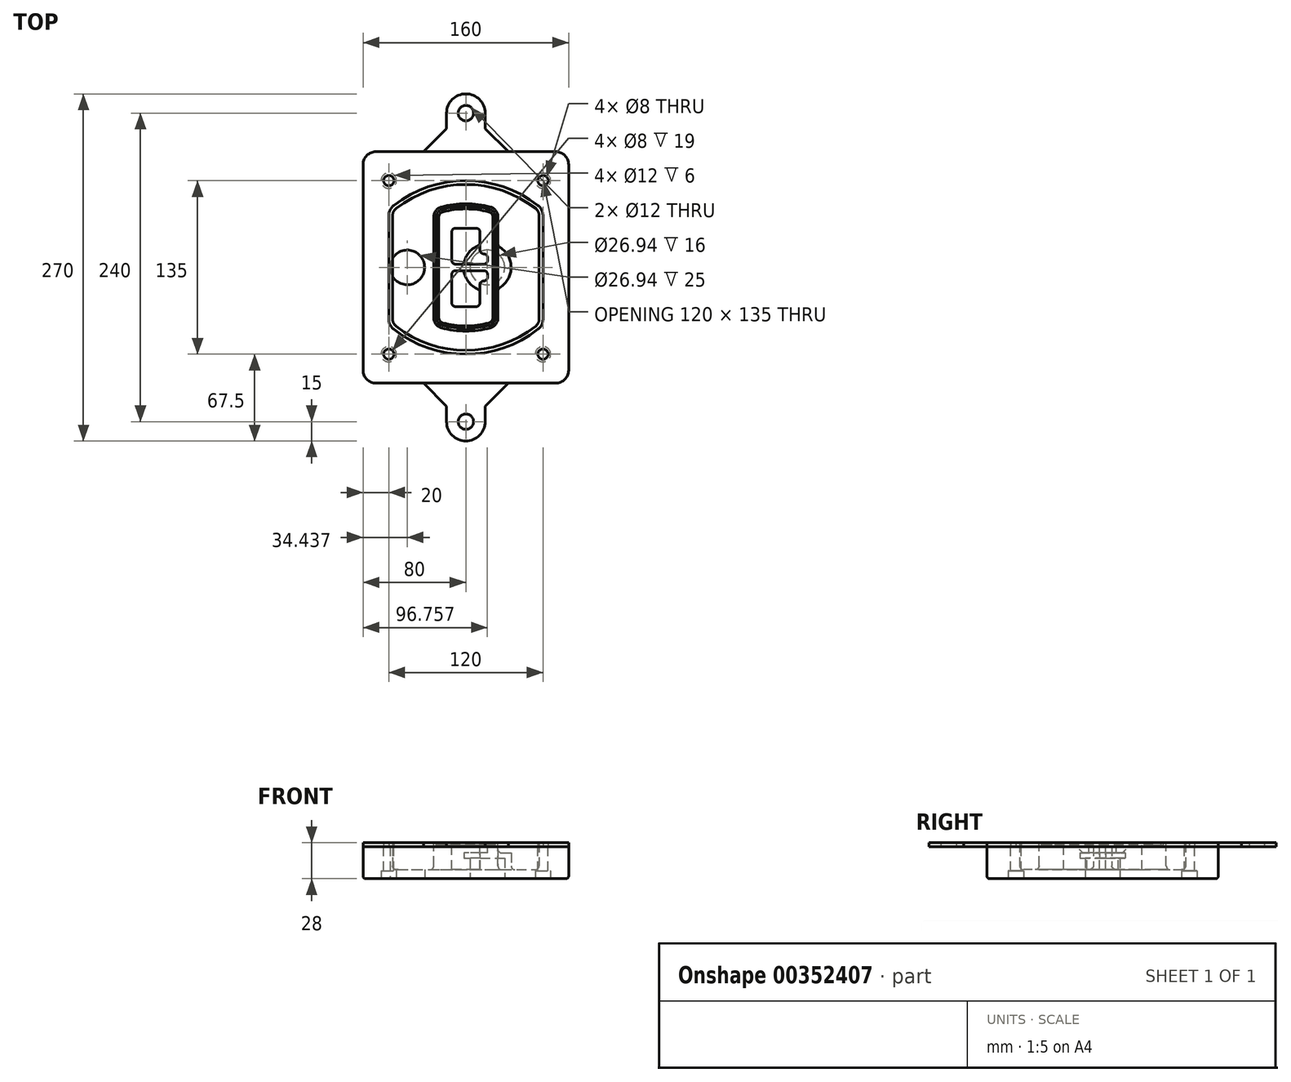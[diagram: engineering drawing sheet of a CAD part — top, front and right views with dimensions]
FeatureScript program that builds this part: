
annotation { "Feature Type Name" : "Feature", "Feature Type Description" : "" }
export const myFeature = defineFeature(function(context is Context, id is Id, definition is map)
    precondition{}
    {
        {
            var Q0;
            Q0=qCreatedBy(makeId("Top.planeOp"),FACE);
            var sketch = newSketch(context, id + "F0", { "sketchPlane" : qUnion([Q0])});
            skPoint(sketch, "E0.rect.middle", {"position": v(0, 0) * mm});
            skLineSegment(sketch, "E1.bottom", {"start": v(-70, -90) * mm, "end": v(70, -90) * mm});
            skLineSegment(sketch, "E1.top", {"start": v(-70, 90) * mm, "end": v(70, 90) * mm});
            skLineSegment(sketch, "E1.left", {"start": v(-80, -80) * mm, "end": v(-80, 80) * mm});
            skLineSegment(sketch, "E1.right", {"start": v(80, -80) * mm, "end": v(80, 80) * mm});
            skLineSegment(sketch, "E2", {"start": v(-80, 90) * mm, "end": v(80, -90) * mm, "construction": true});
            skLineSegment(sketch, "E3", {"start": v(80, 90) * mm, "end": v(-80, -90) * mm, "construction": true});
            skCircle(sketch, "E4", {"center": v(-60, 67.5) * mm, "radius": 4 * mm});
            skCircle(sketch, "E5", {"center": v(60, 67.5) * mm, "radius": 4 * mm});
            skCircle(sketch, "E6", {"center": v(60, -67.5) * mm, "radius": 4 * mm});
            skCircle(sketch, "E7", {"center": v(-60, -67.5) * mm, "radius": 4 * mm});
            skLineSegment(sketch, "E8", {"start": v(-60, 67.5) * mm, "end": v(60, 67.5) * mm, "construction": true});
            skLineSegment(sketch, "E9", {"start": v(60, 67.5) * mm, "end": v(60, -67.5) * mm, "construction": true});
            skLineSegment(sketch, "E10", {"start": v(60, -67.5) * mm, "end": v(-60, -67.5) * mm, "construction": true});
            skLineSegment(sketch, "E11", {"start": v(-60, -67.5) * mm, "end": v(-60, 67.5) * mm, "construction": true});
            skLineSegment(sketch, "E12", {"start": v(-60, 40.3) * mm, "end": v(-60, -40.3) * mm});
            skLineSegment(sketch, "E13", {"start": v(60, 40.3) * mm, "end": v(60, -40.3) * mm});
            skArc(sketch, "E14", {"start": v(56.15, 48.18) * mm, "mid": v(0, 67.5) * mm, "end": v(-56.15, 48.18) * mm});
            skArc(sketch, "E15", {"start": v(-56.15, -48.18) * mm, "mid": v(0, -67.5) * mm, "end": v(56.15, -48.18) * mm});
            skLineSegment(sketch, "E16", {"start": v(-60, 0) * mm, "end": v(60, 0) * mm, "construction": true});
            skPoint(sketch, "E17.visualSharp", {"position": v(-60, -45) * mm});
            skArc(sketch, "E17.filletArc", {"start": v(-60, -40.3) * mm, "mid": v(-58.99, -44.68) * mm, "end": v(-56.15, -48.18) * mm});
            skPoint(sketch, "E18.visualSharp", {"position": v(-60, 45) * mm});
            skArc(sketch, "E18.filletArc", {"start": v(-56.15, 48.18) * mm, "mid": v(-58.99, 44.68) * mm, "end": v(-60, 40.3) * mm});
            skPoint(sketch, "E19.visualSharp", {"position": v(60, 45) * mm});
            skArc(sketch, "E19.filletArc", {"start": v(60, 40.3) * mm, "mid": v(58.99, 44.68) * mm, "end": v(56.15, 48.18) * mm});
            skPoint(sketch, "E20.visualSharp", {"position": v(60, -45) * mm});
            skArc(sketch, "E20.filletArc", {"start": v(56.15, -48.18) * mm, "mid": v(58.99, -44.68) * mm, "end": v(60, -40.3) * mm});
            skPoint(sketch, "E21.visualSharp", {"position": v(-80, 90) * mm});
            skArc(sketch, "E21.filletArc", {"start": v(-70, 90) * mm, "mid": v(-77.07, 87.07) * mm, "end": v(-80, 80) * mm});
            skPoint(sketch, "E22.visualSharp", {"position": v(80, 90) * mm});
            skArc(sketch, "E22.filletArc", {"start": v(80, 80) * mm, "mid": v(77.07, 87.07) * mm, "end": v(70, 90) * mm});
            skPoint(sketch, "E23.visualSharp", {"position": v(80, -90) * mm});
            skArc(sketch, "E23.filletArc", {"start": v(70, -90) * mm, "mid": v(77.07, -87.07) * mm, "end": v(80, -80) * mm});
            skPoint(sketch, "E24.visualSharp", {"position": v(-80, -90) * mm});
            skArc(sketch, "E24.filletArc", {"start": v(-80, -80) * mm, "mid": v(-77.07, -87.07) * mm, "end": v(-70, -90) * mm});
            skArc(sketch, "E25.0", {"start": v(57, 40.3) * mm, "mid": v(56.3, 43.36) * mm, "end": v(54.3, 45.81) * mm});
            skLineSegment(sketch, "E25.1", {"start": v(57, 40.3) * mm, "end": v(57, -40.3) * mm});
            skArc(sketch, "E25.2", {"start": v(54.3, -45.81) * mm, "mid": v(56.3, -43.36) * mm, "end": v(57, -40.3) * mm});
            skArc(sketch, "E25.3", {"start": v(-54.3, -45.81) * mm, "mid": v(0, -64.5) * mm, "end": v(54.3, -45.81) * mm});
            skArc(sketch, "E25.4", {"start": v(-57, -40.3) * mm, "mid": v(-56.3, -43.36) * mm, "end": v(-54.3, -45.81) * mm});
            skArc(sketch, "E25.5", {"start": v(54.3, 45.81) * mm, "mid": v(0, 64.5) * mm, "end": v(-54.3, 45.81) * mm});
            skLineSegment(sketch, "E25.6", {"start": v(-57, 40.3) * mm, "end": v(-57, -40.3) * mm});
            skArc(sketch, "E25.7", {"start": v(-54.3, 45.81) * mm, "mid": v(-56.3, 43.36) * mm, "end": v(-57, 40.3) * mm});
            skArc(sketch, "E26.0", {"start": v(-58.62, 51.33) * mm, "mid": v(-62.58, 46.43) * mm, "end": v(-64, 40.3) * mm});
            skArc(sketch, "E26.1", {"start": v(58.62, 51.33) * mm, "mid": v(0, 71.5) * mm, "end": v(-58.62, 51.33) * mm});
            skArc(sketch, "E26.2", {"start": v(64, 40.3) * mm, "mid": v(62.58, 46.43) * mm, "end": v(58.62, 51.33) * mm});
            skLineSegment(sketch, "E26.3", {"start": v(64, 40.3) * mm, "end": v(64, -40.3) * mm});
            skArc(sketch, "E26.4", {"start": v(58.62, -51.33) * mm, "mid": v(62.58, -46.43) * mm, "end": v(64, -40.3) * mm});
            skLineSegment(sketch, "E26.5", {"start": v(-64, 40.3) * mm, "end": v(-64, -40.3) * mm});
            skArc(sketch, "E26.6", {"start": v(-58.62, -51.33) * mm, "mid": v(0, -71.5) * mm, "end": v(58.62, -51.33) * mm});
            skArc(sketch, "E26.7", {"start": v(-64, -40.3) * mm, "mid": v(-62.58, -46.43) * mm, "end": v(-58.62, -51.33) * mm});
            skSolve(sketch);
        }
        {
            var Q0;
            Q0=makeQuery(id+"F0.imprint","IMPRINT",FACE,{"disambiguationData":[TD([[makeQuery(id+"F0.imprint","IMPRINT",EDGE,{"derivedFrom":sQuery(id+"F0.wireOp",EDGE,"E1.bottom")}),1.0]])]});
            var Q1;
            Q1=makeQuery(id+"F0.imprint","IMPRINT",FACE,{"disambiguationData":[TD([[makeQuery(id+"F0.imprint","IMPRINT",EDGE,{"derivedFrom":sQuery(id+"F0.wireOp",EDGE,"E12")}),1.0]])]});
            var Q2;
            Q2=makeQuery(id+"F0.imprint","IMPRINT",FACE,{"disambiguationData":[TD([[makeQuery(id+"F0.imprint","IMPRINT",EDGE,{"derivedFrom":sQuery(id+"F0.wireOp",EDGE,"E25.0")}),1.0]])]});
            var Q3;
            Q3=makeQuery(id+"F0.imprint","IMPRINT",FACE,{"disambiguationData":[TD([[makeQuery(id+"F0.imprint","IMPRINT",EDGE,{"derivedFrom":sQuery(id+"F0.wireOp",EDGE,"E12")}),-1.0]])]});
            extrude(context, id + "F1", {"entities" : qUnion([Q0, Q1, Q2, Q3]), "oppositeDirection" : true, "depth" : 25 * mm});
        }
        {
            var Q0;
            Q0=makeQuery(id+"F0.imprint","IMPRINT",FACE,{"disambiguationData":[TD([[makeQuery(id+"F0.imprint","IMPRINT",EDGE,{"derivedFrom":sQuery(id+"F0.wireOp",EDGE,"E12")}),1.0]])]});
            extrude(context, id + "F2", {"entities" : qUnion([Q0]), "operationType" : NewBodyOperationType.ADD, "depth" : 3 * mm});
        }
        {
            var Q0;
            Q0=makeQuery(id+"F0.imprint","IMPRINT",FACE,{"disambiguationData":[TD([[makeQuery(id+"F0.imprint","IMPRINT",EDGE,{"derivedFrom":sQuery(id+"F0.wireOp",EDGE,"E25.0")}),1.0]])]});
            extrude(context, id + "F3", {"entities" : qUnion([Q0]), "operationType" : NewBodyOperationType.REMOVE, "oppositeDirection" : true, "depth" : 18 * mm});
        }
        {
            var Q0;
            Q0=makeQuery(id+"F2.opExtrude","CAP_FACE",FACE,{"disambiguationData":[OSD([sQuery(id+"F0.wireOp",EDGE,"E12"),sQuery(id+"F0.wireOp",EDGE,"E13"),sQuery(id+"F0.wireOp",EDGE,"E14"),sQuery(id+"F0.wireOp",EDGE,"E15"),sQuery(id+"F0.wireOp",EDGE,"E17.filletArc"),sQuery(id+"F0.wireOp",EDGE,"E18.filletArc"),sQuery(id+"F0.wireOp",EDGE,"E19.filletArc"),sQuery(id+"F0.wireOp",EDGE,"E20.filletArc"),sQuery(id+"F0.wireOp",EDGE,"E25.0"),sQuery(id+"F0.wireOp",EDGE,"E25.1"),sQuery(id+"F0.wireOp",EDGE,"E25.2"),sQuery(id+"F0.wireOp",EDGE,"E25.3"),sQuery(id+"F0.wireOp",EDGE,"E25.4"),sQuery(id+"F0.wireOp",EDGE,"E25.5"),sQuery(id+"F0.wireOp",EDGE,"E25.6"),sQuery(id+"F0.wireOp",EDGE,"E25.7")])],"isStart":false});
            var sketch = newSketch(context, id + "F4", { "sketchPlane" : qUnion([Q0])});
            skArc(sketch, "E27.0", {"start": v(-19.08, -46.97) * mm, "mid": v(0, -49.5) * mm, "end": v(19.08, -46.97) * mm});
            skArc(sketch, "E28.0", {"start": v(19.08, 46.97) * mm, "mid": v(0, 49.5) * mm, "end": v(-19.08, 46.97) * mm});
            skLineSegment(sketch, "E29", {"start": v(-25, 39.25) * mm, "end": v(-25, -39.25) * mm});
            skLineSegment(sketch, "E30", {"start": v(25, 39.25) * mm, "end": v(25, -39.25) * mm});
            skLineSegment(sketch, "E31", {"start": v(-25, 45.1) * mm, "end": v(25, 45.1) * mm, "construction": true});
            skLineSegment(sketch, "E32", {"start": v(-25, -45.1) * mm, "end": v(25, -45.1) * mm, "construction": true});
            skPoint(sketch, "E33.visualSharp", {"position": v(-25, 45.1) * mm});
            skArc(sketch, "E33.filletArc", {"start": v(-19.08, 46.97) * mm, "mid": v(-23.35, 44.11) * mm, "end": v(-25, 39.25) * mm});
            skPoint(sketch, "E34.visualSharp", {"position": v(25, 45.1) * mm});
            skArc(sketch, "E34.filletArc", {"start": v(25, 39.25) * mm, "mid": v(23.35, 44.11) * mm, "end": v(19.08, 46.97) * mm});
            skPoint(sketch, "E35.visualSharp", {"position": v(25, -45.1) * mm});
            skArc(sketch, "E35.filletArc", {"start": v(19.08, -46.97) * mm, "mid": v(23.35, -44.11) * mm, "end": v(25, -39.25) * mm});
            skPoint(sketch, "E36.visualSharp", {"position": v(-25, -45.1) * mm});
            skArc(sketch, "E36.filletArc", {"start": v(-25, -39.25) * mm, "mid": v(-23.35, -44.11) * mm, "end": v(-19.08, -46.97) * mm});
            skArc(sketch, "E37.0", {"start": v(54.3, 45.81) * mm, "mid": v(0, 64.5) * mm, "end": v(-54.3, 45.81) * mm});
            skArc(sketch, "E37.1", {"start": v(-54.3, 45.81) * mm, "mid": v(-56.3, 43.36) * mm, "end": v(-57, 40.3) * mm});
            skLineSegment(sketch, "E37.2", {"start": v(-57, 40.3) * mm, "end": v(-57, -40.3) * mm});
            skArc(sketch, "E37.3", {"start": v(-57, -40.3) * mm, "mid": v(-56.3, -43.36) * mm, "end": v(-54.3, -45.81) * mm});
            skArc(sketch, "E37.4", {"start": v(-54.3, -45.81) * mm, "mid": v(0, -64.5) * mm, "end": v(54.3, -45.81) * mm});
            skArc(sketch, "E37.5", {"start": v(54.3, -45.81) * mm, "mid": v(56.3, -43.36) * mm, "end": v(57, -40.3) * mm});
            skLineSegment(sketch, "E37.6", {"start": v(57, 40.3) * mm, "end": v(57, -40.3) * mm});
            skArc(sketch, "E37.7", {"start": v(57, 40.3) * mm, "mid": v(56.3, 43.36) * mm, "end": v(54.3, 45.81) * mm});
            skLineSegment(sketch, "E38.0", {"start": v(23, 39.25) * mm, "end": v(23, -39.25) * mm});
            skArc(sketch, "E38.1", {"start": v(18.56, -45.04) * mm, "mid": v(21.76, -42.9) * mm, "end": v(23, -39.25) * mm});
            skArc(sketch, "E38.2", {"start": v(-18.56, -45.04) * mm, "mid": v(0, -47.5) * mm, "end": v(18.56, -45.04) * mm});
            skArc(sketch, "E38.3", {"start": v(-23, -39.25) * mm, "mid": v(-21.76, -42.9) * mm, "end": v(-18.56, -45.04) * mm});
            skLineSegment(sketch, "E38.4", {"start": v(-23, 39.25) * mm, "end": v(-23, -39.25) * mm});
            skArc(sketch, "E38.5", {"start": v(23, 39.25) * mm, "mid": v(21.76, 42.9) * mm, "end": v(18.56, 45.04) * mm});
            skArc(sketch, "E38.6", {"start": v(-18.56, 45.04) * mm, "mid": v(-21.76, 42.9) * mm, "end": v(-23, 39.25) * mm});
            skArc(sketch, "E38.7", {"start": v(18.56, 45.04) * mm, "mid": v(0, 47.5) * mm, "end": v(-18.56, 45.04) * mm});
            skArc(sketch, "E39.0", {"start": v(21, 39.25) * mm, "mid": v(20.18, 41.68) * mm, "end": v(18.04, 43.1) * mm});
            skLineSegment(sketch, "E39.1", {"start": v(21, 39.25) * mm, "end": v(21, -39.25) * mm});
            skArc(sketch, "E39.2", {"start": v(18.04, -43.1) * mm, "mid": v(20.18, -41.68) * mm, "end": v(21, -39.25) * mm});
            skArc(sketch, "E39.3", {"start": v(-18.04, -43.1) * mm, "mid": v(0, -45.5) * mm, "end": v(18.04, -43.1) * mm});
            skArc(sketch, "E39.4", {"start": v(-21, -39.25) * mm, "mid": v(-20.18, -41.68) * mm, "end": v(-18.04, -43.1) * mm});
            skArc(sketch, "E39.5", {"start": v(18.04, 43.1) * mm, "mid": v(0, 45.5) * mm, "end": v(-18.04, 43.1) * mm});
            skLineSegment(sketch, "E39.6", {"start": v(-21, 39.25) * mm, "end": v(-21, -39.25) * mm});
            skArc(sketch, "E39.7", {"start": v(-18.04, 43.1) * mm, "mid": v(-20.18, 41.68) * mm, "end": v(-21, 39.25) * mm});
            skLineSegment(sketch, "E40", {"start": v(-25, 0) * mm, "end": v(25, 0) * mm, "construction": true});
            skLineSegment(sketch, "E41", {"start": v(-11, 5.5) * mm, "end": v(-11, 27.5) * mm});
            skLineSegment(sketch, "E42", {"start": v(-8, 30.5) * mm, "end": v(8, 30.5) * mm});
            skLineSegment(sketch, "E43", {"start": v(11, 27.5) * mm, "end": v(11, 13.5) * mm});
            skLineSegment(sketch, "E44", {"start": v(14, 10.5) * mm, "end": v(14, 10.5) * mm});
            skLineSegment(sketch, "E45", {"start": v(17, 7.5) * mm, "end": v(17, 5.5) * mm});
            skLineSegment(sketch, "E46", {"start": v(14, 2.5) * mm, "end": v(-8, 2.5) * mm});
            skPoint(sketch, "E47.visualSharp", {"position": v(-11, 30.5) * mm});
            skArc(sketch, "E47.filletArc", {"start": v(-8, 30.5) * mm, "mid": v(-10.12, 29.62) * mm, "end": v(-11, 27.5) * mm});
            skPoint(sketch, "E48.visualSharp", {"position": v(11, 30.5) * mm});
            skArc(sketch, "E48.filletArc", {"start": v(11, 27.5) * mm, "mid": v(10.12, 29.62) * mm, "end": v(8, 30.5) * mm});
            skPoint(sketch, "E49.visualSharp", {"position": v(11, 10.5) * mm});
            skArc(sketch, "E49.filletArc", {"start": v(11, 13.5) * mm, "mid": v(11.88, 11.38) * mm, "end": v(14, 10.5) * mm});
            skPoint(sketch, "E50.visualSharp", {"position": v(17, 10.5) * mm});
            skArc(sketch, "E50.filletArc", {"start": v(17, 7.5) * mm, "mid": v(16.12, 9.62) * mm, "end": v(14, 10.5) * mm});
            skPoint(sketch, "E51.visualSharp", {"position": v(17, 2.5) * mm});
            skArc(sketch, "E51.filletArc", {"start": v(14, 2.5) * mm, "mid": v(16.12, 3.38) * mm, "end": v(17, 5.5) * mm});
            skPoint(sketch, "E52.visualSharp", {"position": v(-11, 2.5) * mm});
            skArc(sketch, "E52.filletArc", {"start": v(-11, 5.5) * mm, "mid": v(-10.12, 3.38) * mm, "end": v(-8, 2.5) * mm});
            skLineSegment(sketch, "E53.0.MirrorCS", {"start": v(14, -2.5) * mm, "end": v(-8, -2.5) * mm});
            skArc(sketch, "E54.0.MirrorCS", {"start": v(-11, -5.5) * mm, "mid": v(-10.12, -3.38) * mm, "end": v(-8, -2.5) * mm});
            skLineSegment(sketch, "E55.0.MirrorCS", {"start": v(-11, -5.5) * mm, "end": v(-11, -27.5) * mm});
            skArc(sketch, "E56.0.MirrorCS", {"start": v(-8, -30.5) * mm, "mid": v(-10.12, -29.62) * mm, "end": v(-11, -27.5) * mm});
            skLineSegment(sketch, "E57.0.MirrorCS", {"start": v(-8, -30.5) * mm, "end": v(8, -30.5) * mm});
            skArc(sketch, "E58.0.MirrorCS", {"start": v(11, -27.5) * mm, "mid": v(10.12, -29.62) * mm, "end": v(8, -30.5) * mm});
            skLineSegment(sketch, "E59.0.MirrorCS", {"start": v(11, -27.5) * mm, "end": v(11, -13.5) * mm});
            skArc(sketch, "E60.0.MirrorCS", {"start": v(11, -13.5) * mm, "mid": v(11.88, -11.38) * mm, "end": v(14, -10.5) * mm});
            skArc(sketch, "E61.0.MirrorCS", {"start": v(17, -7.5) * mm, "mid": v(16.12, -9.62) * mm, "end": v(14, -10.5) * mm});
            skLineSegment(sketch, "E62.0.MirrorCS", {"start": v(17, -7.5) * mm, "end": v(17, -5.5) * mm});
            skArc(sketch, "E63.0.MirrorCS", {"start": v(14, -2.5) * mm, "mid": v(16.12, -3.38) * mm, "end": v(17, -5.5) * mm});
            skSolve(sketch);
        }
        {
            var Q0;
            Q0=makeQuery(id+"F4.imprint","IMPRINT",FACE,{"disambiguationData":[TD([[makeQuery(id+"F4.imprint","IMPRINT",EDGE,{"derivedFrom":sQuery(id+"F4.wireOp",EDGE,"E27.0")}),1.0]])]});
            var Q1;
            Q1=makeQuery(id+"F4.imprint","IMPRINT",FACE,{"disambiguationData":[TD([[makeQuery(id+"F4.imprint","IMPRINT",EDGE,{"derivedFrom":sQuery(id+"F4.wireOp",EDGE,"E38.0")}),-1.0]])]});
            var Q2;
            Q2=makeQuery(id+"F4.imprint","IMPRINT",FACE,{"disambiguationData":[TD([[makeQuery(id+"F4.imprint","IMPRINT",EDGE,{"derivedFrom":sQuery(id+"F4.wireOp",EDGE,"E39.0")}),1.0]])]});
            extrude(context, id + "F5", {"entities" : qUnion([Q0, Q1, Q2]), "operationType" : NewBodyOperationType.ADD, "endBound" : BoundingType.UP_TO_NEXT, "oppositeDirection" : true, "depth" : 25 * mm});
        }
        {
            var Q0;
            Q0=makeQuery(id+"F4.imprint","IMPRINT",FACE,{"disambiguationData":[TD([[makeQuery(id+"F4.imprint","IMPRINT",EDGE,{"derivedFrom":sQuery(id+"F4.wireOp",EDGE,"E38.0")}),-1.0]])]});
            extrude(context, id + "F6", {"entities" : qUnion([Q0]), "operationType" : NewBodyOperationType.REMOVE, "oppositeDirection" : true, "depth" : 2 * mm});
        }
        {
            var Q0;
            Q0=makeQuery(id+"F1.opExtrude","CAP_FACE",FACE,{"disambiguationData":[OSD([sQuery(id+"F0.wireOp",EDGE,"E1.bottom"),sQuery(id+"F0.wireOp",EDGE,"E1.top"),sQuery(id+"F0.wireOp",EDGE,"E1.left"),sQuery(id+"F0.wireOp",EDGE,"E1.right"),sQuery(id+"F0.wireOp",EDGE,"E4"),sQuery(id+"F0.wireOp",EDGE,"E5"),sQuery(id+"F0.wireOp",EDGE,"E6"),sQuery(id+"F0.wireOp",EDGE,"E7"),sQuery(id+"F0.wireOp",EDGE,"E21.filletArc"),sQuery(id+"F0.wireOp",EDGE,"E22.filletArc"),sQuery(id+"F0.wireOp",EDGE,"E23.filletArc"),sQuery(id+"F0.wireOp",EDGE,"E24.filletArc")])],"isStart":false});
            var sketch = newSketch(context, id + "F7", { "sketchPlane" : qUnion([Q0])});
            skCircle(sketch, "E64", {"center": v(16.76, 0) * mm, "radius": 13.47 * mm});
            skCircle(sketch, "E65", {"center": v(-45.56, 0) * mm, "radius": 13.47 * mm});
            skLineSegment(sketch, "E66", {"start": v(80, 0) * mm, "end": v(-80, 0) * mm});
            skCircle(sketch, "E67", {"center": v(16.76, 0) * mm, "radius": 18.47 * mm});
            skCircle(sketch, "E68", {"center": v(60, -67.5) * mm, "radius": 6 * mm});
            skCircle(sketch, "E69", {"center": v(-60, -67.5) * mm, "radius": 6 * mm});
            skCircle(sketch, "E70", {"center": v(-60, 67.5) * mm, "radius": 6 * mm});
            skCircle(sketch, "E71", {"center": v(60, 67.5) * mm, "radius": 6 * mm});
            skSolve(sketch);
        }
        {
            var Q0;
            {var subQ1=sQuery(id+"F7.wireOp",EDGE,"E66");var subQ4=sQuery(id+"F7.wireOp",EDGE,"E64");var subQ6=makeQuery(id+"F7.imprint","INTERSECT",VERTEX,{"disambiguationData":[OD(0.0)],"derivedFrom":[subQ4,subQ1]});Q0=makeQuery(id+"F7.imprint","IMPRINT",FACE,{"disambiguationData":[TD([[makeQuery(id+"F7.imprint","IMPRINT",EDGE,{"disambiguationData":[TD([[subQ6,-1.0]])],"derivedFrom":subQ4}),-1.0]])]});}
            var Q1;
            {var subQ0=sQuery(id+"F7.wireOp",EDGE,"E66");var subQ1=sQuery(id+"F7.wireOp",EDGE,"E64");var subQ3=makeQuery(id+"F7.imprint","INTERSECT",VERTEX,{"disambiguationData":[OD(0.0)],"derivedFrom":[subQ1,subQ0]});Q1=makeQuery(id+"F7.imprint","IMPRINT",FACE,{"disambiguationData":[TD([[makeQuery(id+"F7.imprint","IMPRINT",EDGE,{"disambiguationData":[TD([[subQ3,-1.0]])],"derivedFrom":subQ1}),1.0]])]});}
            var Q2;
            {var subQ0=sQuery(id+"F7.wireOp",EDGE,"E66");var subQ1=sQuery(id+"F7.wireOp",EDGE,"E64");var subQ3=makeQuery(id+"F7.imprint","INTERSECT",VERTEX,{"disambiguationData":[OD(0.0)],"derivedFrom":[subQ1,subQ0]});Q2=makeQuery(id+"F7.imprint","IMPRINT",FACE,{"disambiguationData":[TD([[makeQuery(id+"F7.imprint","IMPRINT",EDGE,{"disambiguationData":[TD([[subQ3,1.0]])],"derivedFrom":subQ1}),1.0]])]});}
            var Q3;
            {var subQ1=sQuery(id+"F7.wireOp",EDGE,"E66");var subQ4=sQuery(id+"F7.wireOp",EDGE,"E64");var subQ6=makeQuery(id+"F7.imprint","INTERSECT",VERTEX,{"disambiguationData":[OD(0.0)],"derivedFrom":[subQ4,subQ1]});Q3=makeQuery(id+"F7.imprint","IMPRINT",FACE,{"disambiguationData":[TD([[makeQuery(id+"F7.imprint","IMPRINT",EDGE,{"disambiguationData":[TD([[subQ6,1.0]])],"derivedFrom":subQ4}),-1.0]])]});}
            extrude(context, id + "F8", {"entities" : qUnion([Q0, Q1, Q2, Q3]), "operationType" : NewBodyOperationType.ADD, "oppositeDirection" : true, "depth" : 20 * mm});
        }
        {
            var Q0;
            {var subQ0=sQuery(id+"F7.wireOp",EDGE,"E66");var subQ1=sQuery(id+"F7.wireOp",EDGE,"E64");var subQ3=makeQuery(id+"F7.imprint","INTERSECT",VERTEX,{"disambiguationData":[OD(0.0)],"derivedFrom":[subQ1,subQ0]});Q0=makeQuery(id+"F7.imprint","IMPRINT",FACE,{"disambiguationData":[TD([[makeQuery(id+"F7.imprint","IMPRINT",EDGE,{"disambiguationData":[TD([[subQ3,-1.0]])],"derivedFrom":subQ1}),1.0]])]});}
            var Q1;
            {var subQ0=sQuery(id+"F7.wireOp",EDGE,"E66");var subQ1=sQuery(id+"F7.wireOp",EDGE,"E64");var subQ3=makeQuery(id+"F7.imprint","INTERSECT",VERTEX,{"disambiguationData":[OD(0.0)],"derivedFrom":[subQ1,subQ0]});Q1=makeQuery(id+"F7.imprint","IMPRINT",FACE,{"disambiguationData":[TD([[makeQuery(id+"F7.imprint","IMPRINT",EDGE,{"disambiguationData":[TD([[subQ3,1.0]])],"derivedFrom":subQ1}),1.0]])]});}
            extrude(context, id + "F9", {"entities" : qUnion([Q0, Q1]), "operationType" : NewBodyOperationType.REMOVE, "oppositeDirection" : true, "depth" : 16 * mm});
        }
        {
            var Q0;
            {var subQ0=sQuery(id+"F7.wireOp",EDGE,"E66");var subQ1=sQuery(id+"F7.wireOp",EDGE,"E65");var subQ3=makeQuery(id+"F7.imprint","INTERSECT",VERTEX,{"disambiguationData":[OD(0.0)],"derivedFrom":[subQ1,subQ0]});Q0=makeQuery(id+"F7.imprint","IMPRINT",FACE,{"disambiguationData":[TD([[makeQuery(id+"F7.imprint","IMPRINT",EDGE,{"disambiguationData":[TD([[subQ3,-1.0]])],"derivedFrom":subQ1}),1.0]])]});}
            var Q1;
            {var subQ0=sQuery(id+"F7.wireOp",EDGE,"E66");var subQ1=sQuery(id+"F7.wireOp",EDGE,"E65");var subQ3=makeQuery(id+"F7.imprint","INTERSECT",VERTEX,{"disambiguationData":[OD(0.0)],"derivedFrom":[subQ1,subQ0]});Q1=makeQuery(id+"F7.imprint","IMPRINT",FACE,{"disambiguationData":[TD([[makeQuery(id+"F7.imprint","IMPRINT",EDGE,{"disambiguationData":[TD([[subQ3,1.0]])],"derivedFrom":subQ1}),1.0]])]});}
            extrude(context, id + "F10", {"entities" : qUnion([Q0, Q1]), "operationType" : NewBodyOperationType.REMOVE, "oppositeDirection" : true, "depth" : 25 * mm});
        }
        {
            var Q0;
            Q0=makeQuery(id+"F7.imprint","IMPRINT",FACE,{"disambiguationData":[TD([[makeQuery(id+"F7.imprint","IMPRINT",EDGE,{"derivedFrom":sQuery(id+"F7.wireOp",EDGE,"E68")}),1.0]])]});
            var Q1;
            Q1=makeQuery(id+"F7.imprint","IMPRINT",FACE,{"disambiguationData":[TD([[makeQuery(id+"F7.imprint","IMPRINT",EDGE,{"derivedFrom":makeQuery(id+"F1.opExtrude","CAP_EDGE",EDGE,{"disambiguationData":[OSD([sQuery(id+"F0.wireOp",EDGE,"E5")])],"isStart":false})}),-1.0]])]});
            var Q2;
            Q2=makeQuery(id+"F7.imprint","IMPRINT",FACE,{"disambiguationData":[TD([[makeQuery(id+"F7.imprint","IMPRINT",EDGE,{"derivedFrom":sQuery(id+"F7.wireOp",EDGE,"E69")}),1.0]])]});
            var Q3;
            Q3=makeQuery(id+"F7.imprint","IMPRINT",FACE,{"disambiguationData":[TD([[makeQuery(id+"F7.imprint","IMPRINT",EDGE,{"derivedFrom":makeQuery(id+"F1.opExtrude","CAP_EDGE",EDGE,{"disambiguationData":[OSD([sQuery(id+"F0.wireOp",EDGE,"E4")])],"isStart":false})}),-1.0]])]});
            var Q4;
            Q4=makeQuery(id+"F7.imprint","IMPRINT",FACE,{"disambiguationData":[TD([[makeQuery(id+"F7.imprint","IMPRINT",EDGE,{"derivedFrom":sQuery(id+"F7.wireOp",EDGE,"E70")}),1.0]])]});
            var Q5;
            Q5=makeQuery(id+"F7.imprint","IMPRINT",FACE,{"disambiguationData":[TD([[makeQuery(id+"F7.imprint","IMPRINT",EDGE,{"derivedFrom":makeQuery(id+"F1.opExtrude","CAP_EDGE",EDGE,{"disambiguationData":[OSD([sQuery(id+"F0.wireOp",EDGE,"E7")])],"isStart":false})}),-1.0]])]});
            var Q6;
            Q6=makeQuery(id+"F7.imprint","IMPRINT",FACE,{"disambiguationData":[TD([[makeQuery(id+"F7.imprint","IMPRINT",EDGE,{"derivedFrom":sQuery(id+"F7.wireOp",EDGE,"E71")}),1.0]])]});
            var Q7;
            Q7=makeQuery(id+"F7.imprint","IMPRINT",FACE,{"disambiguationData":[TD([[makeQuery(id+"F7.imprint","IMPRINT",EDGE,{"derivedFrom":makeQuery(id+"F1.opExtrude","CAP_EDGE",EDGE,{"disambiguationData":[OSD([sQuery(id+"F0.wireOp",EDGE,"E6")])],"isStart":false})}),-1.0]])]});
            extrude(context, id + "F11", {"entities" : qUnion([Q0, Q1, Q2, Q3, Q4, Q5, Q6, Q7]), "operationType" : NewBodyOperationType.REMOVE, "oppositeDirection" : true, "depth" : 6 * mm});
        }
        {
            var Q0;
            Q0=makeQuery(id+"F9.boolean.opBoolean","COPY",FACE,{"derivedFrom":makeQuery(id+"F9.opExtrude","CAP_FACE",FACE,{"disambiguationData":[OSD([sQuery(id+"F7.wireOp",EDGE,"E64")])],"isStart":false})});
            var sketch = newSketch(context, id + "F12", { "sketchPlane" : qUnion([Q0])});
            skArc(sketch, "E72.0", {"start": v(11, 17.55) * mm, "mid": v(2.57, 11.82) * mm, "end": v(-1.54, 2.5) * mm});
            skArc(sketch, "E72.1", {"start": v(-1.54, -2.5) * mm, "mid": v(2.57, -11.82) * mm, "end": v(11, -17.55) * mm});
            skLineSegment(sketch, "E73", {"start": v(-1.54, -2.5) * mm, "end": v(14, -2.5) * mm});
            skLineSegment(sketch, "E74.0", {"start": v(14, 2.5) * mm, "end": v(-1.54, 2.5) * mm});
            skArc(sketch, "E74.1", {"start": v(14, 2.5) * mm, "mid": v(16.12, 3.38) * mm, "end": v(17, 5.5) * mm});
            skLineSegment(sketch, "E74.2", {"start": v(17, 7.5) * mm, "end": v(17, 5.5) * mm});
            skArc(sketch, "E74.3", {"start": v(17, 7.5) * mm, "mid": v(16.12, 9.62) * mm, "end": v(14, 10.5) * mm});
            skArc(sketch, "E74.4", {"start": v(11, 13.5) * mm, "mid": v(11.88, 11.38) * mm, "end": v(14, 10.5) * mm});
            skLineSegment(sketch, "E74.5", {"start": v(11, 17.55) * mm, "end": v(11, 13.5) * mm});
            skLineSegment(sketch, "E74.7", {"start": v(14, -2.5) * mm, "end": v(-1.54, -2.5) * mm});
            skArc(sketch, "E74.8", {"start": v(14, -2.5) * mm, "mid": v(16.12, -3.38) * mm, "end": v(17, -5.5) * mm});
            skLineSegment(sketch, "E74.9", {"start": v(17, -7.5) * mm, "end": v(17, -5.5) * mm});
            skArc(sketch, "E74.10", {"start": v(17, -7.5) * mm, "mid": v(16.12, -9.62) * mm, "end": v(14, -10.5) * mm});
            skArc(sketch, "E74.11", {"start": v(11, -13.5) * mm, "mid": v(11.88, -11.38) * mm, "end": v(14, -10.5) * mm});
            skLineSegment(sketch, "E74.12", {"start": v(11, -17.55) * mm, "end": v(11, -13.5) * mm});
            skPoint(sketch, "E75.orphan", {"position": v(11, -27.5) * mm});
            skPoint(sketch, "E76.orphan", {"position": v(-8, -2.5) * mm});
            skPoint(sketch, "E77.orphan", {"position": v(-8, 2.5) * mm});
            skPoint(sketch, "E78.orphan", {"position": v(11, 27.5) * mm});
            skSolve(sketch);
        }
        {
            var Q0;
            {var subQ7=sQuery(id+"F12.wireOp",EDGE,"E72.0");var subQ14=sQuery(id+"F12.wireOp",EDGE,"E72.1");var subQ16=sQuery(id+"F12.wireOp",EDGE,"E74.1");var subQ18=sQuery(id+"F12.wireOp",EDGE,"E74.8");Q0=qUnion([makeQuery(id+"F12.imprint","IMPRINT",FACE,{"disambiguationData":[TD([[makeQuery(id+"F12.imprint","IMPRINT",EDGE,{"derivedFrom":subQ7}),1.0]])]}),makeQuery(id+"F12.imprint","IMPRINT",FACE,{"disambiguationData":[TD([[makeQuery(id+"F12.imprint","IMPRINT",EDGE,{"derivedFrom":subQ14}),1.0]])]}),makeQuery(id+"F12.imprint","IMPRINT",FACE,{"disambiguationData":[TD([[makeQuery(id+"F12.imprint","IMPRINT",EDGE,{"derivedFrom":subQ16}),1.0]])]}),makeQuery(id+"F12.imprint","IMPRINT",FACE,{"disambiguationData":[TD([[makeQuery(id+"F12.imprint","IMPRINT",EDGE,{"derivedFrom":subQ18}),-1.0]])]})]);}
            var Q1;
            Q1=makeQuery(id+"F5.boolean.opBoolean","SPLIT",FACE,{"disambiguationData":[TD([makeQuery(id+"F5.opExtrude","SWEPT_FACE",FACE,{"disambiguationData":[OSD([sQuery(id+"F4.wireOp",EDGE,"E41")])]})])],"derivedFrom":makeQuery(id+"F3.boolean.opBoolean","COPY",FACE,{"derivedFrom":makeQuery(id+"F3.opExtrude","CAP_FACE",FACE,{"disambiguationData":[OSD([sQuery(id+"F0.wireOp",EDGE,"E25.0"),sQuery(id+"F0.wireOp",EDGE,"E25.1"),sQuery(id+"F0.wireOp",EDGE,"E25.2"),sQuery(id+"F0.wireOp",EDGE,"E25.3"),sQuery(id+"F0.wireOp",EDGE,"E25.4"),sQuery(id+"F0.wireOp",EDGE,"E25.5"),sQuery(id+"F0.wireOp",EDGE,"E25.6"),sQuery(id+"F0.wireOp",EDGE,"E25.7")])],"isStart":false})})});
            extrude(context, id + "F13", {"entities" : qUnion([Q0]), "operationType" : NewBodyOperationType.REMOVE, "endBound" : BoundingType.UP_TO_SURFACE, "endBoundEntityFace" : qUnion([Q1]), "depth" : 25 * mm});
        }
        {
            var Q0;
            Q0=makeQuery(id+"F3.boolean.opBoolean","COPY",EDGE,{"derivedFrom":makeQuery(id+"F3.opExtrude","CAP_EDGE",EDGE,{"disambiguationData":[OSD([sQuery(id+"F0.wireOp",EDGE,"E25.6")])],"isStart":false})});
            var Q1;
            Q1=makeQuery(id+"F8.boolean.opBoolean","INTERSECT",EDGE,{"derivedFrom":[makeQuery(id+"F5.opExtrude","SWEPT_FACE",FACE,{"disambiguationData":[OSD([sQuery(id+"F4.wireOp",EDGE,"E30")])]}),makeQuery(id+"F8.opExtrude","CAP_FACE",FACE,{"disambiguationData":[OSD([sQuery(id+"F7.wireOp",EDGE,"E67")])],"isStart":false})]});
            var Q2;
            Q2=makeQuery(id+"F8.boolean.opBoolean","INTERSECT",EDGE,{"disambiguationData":[OD(1.0)],"derivedFrom":[makeQuery(id+"F5.opExtrude","SWEPT_FACE",FACE,{"disambiguationData":[OSD([sQuery(id+"F4.wireOp",EDGE,"E30")])]}),makeQuery(id+"F8.opExtrude","SWEPT_FACE",FACE,{"disambiguationData":[OSD([sQuery(id+"F7.wireOp",EDGE,"E67")])]})]});
            var Q3;
            {var subQ0=sQuery(id+"F4.wireOp",EDGE,"E30");Q3=makeQuery(id+"F8.boolean.opBoolean","SPLIT",EDGE,{"disambiguationData":[TD([makeQuery(id+"F5.opExtrude","SWEPT_FACE",FACE,{"disambiguationData":[OSD([sQuery(id+"F4.wireOp",EDGE,"E35.filletArc")])]})])],"derivedFrom":makeQuery(id+"F5.opExtrude","CAP_EDGE",EDGE,{"disambiguationData":[OSD([subQ0])],"isStart":false})});}
            var Q4;
            {var subQ0=sQuery(id+"F0.wireOp",EDGE,"E25.7");var subQ1=sQuery(id+"F0.wireOp",EDGE,"E25.1");var subQ2=sQuery(id+"F0.wireOp",EDGE,"E25.6");var subQ3=sQuery(id+"F0.wireOp",EDGE,"E25.5");var subQ4=sQuery(id+"F0.wireOp",EDGE,"E25.4");var subQ5=sQuery(id+"F0.wireOp",EDGE,"E25.0");var subQ6=sQuery(id+"F0.wireOp",EDGE,"E25.2");var subQ7=sQuery(id+"F0.wireOp",EDGE,"E25.3");Q4=makeQuery(id+"F8.boolean.opBoolean","INTERSECT",EDGE,{"derivedFrom":[makeQuery(id+"F5.boolean.opBoolean","SPLIT",FACE,{"disambiguationData":[TD([makeQuery(id+"F2.opExtrude","SWEPT_FACE",FACE,{"disambiguationData":[OSD([subQ5])]})])],"derivedFrom":makeQuery(id+"F3.boolean.opBoolean","COPY",FACE,{"derivedFrom":makeQuery(id+"F3.opExtrude","CAP_FACE",FACE,{"disambiguationData":[OSD([subQ5,subQ1,subQ6,subQ7,subQ4,subQ3,subQ2,subQ0])],"isStart":false})})}),makeQuery(id+"F8.opExtrude","SWEPT_FACE",FACE,{"disambiguationData":[OSD([sQuery(id+"F7.wireOp",EDGE,"E67")])]})]});}
            var Q5;
            Q5=makeQuery(id+"F8.boolean.opBoolean","INTERSECT",EDGE,{"disambiguationData":[OD(0.0)],"derivedFrom":[makeQuery(id+"F5.opExtrude","SWEPT_FACE",FACE,{"disambiguationData":[OSD([sQuery(id+"F4.wireOp",EDGE,"E30")])]}),makeQuery(id+"F8.opExtrude","SWEPT_FACE",FACE,{"disambiguationData":[OSD([sQuery(id+"F7.wireOp",EDGE,"E67")])]})]});
            fillet(context, id + "F14", {"entities" : qUnion([Q0, Q1, Q2, Q3, Q4, Q5]), "radius" : 3 * mm, "tangentPropagation" : true, "allowEdgeOverflow" : false});
        }
        {
            var Q0;
            Q0=makeQuery(id+"F1.opExtrude","CAP_EDGE",EDGE,{"disambiguationData":[OSD([sQuery(id+"F0.wireOp",EDGE,"E1.bottom")])],"isStart":false});
            fillet(context, id + "F15", {"entities" : qUnion([Q0]), "radius" : 2 * mm, "tangentPropagation" : true, "allowEdgeOverflow" : false});
        }
        {
            var Q0;
            {var subQ0=sQuery(id+"F0.wireOp",EDGE,"E21.filletArc");var subQ1=sQuery(id+"F0.wireOp",EDGE,"E7");var subQ2=sQuery(id+"F0.wireOp",EDGE,"E6");var subQ3=sQuery(id+"F0.wireOp",EDGE,"E5");var subQ4=sQuery(id+"F0.wireOp",EDGE,"E4");var subQ5=sQuery(id+"F0.wireOp",EDGE,"E22.filletArc");var subQ6=sQuery(id+"F0.wireOp",EDGE,"E1.bottom");var subQ7=sQuery(id+"F0.wireOp",EDGE,"E1.right");var subQ8=sQuery(id+"F0.wireOp",EDGE,"E1.top");var subQ9=sQuery(id+"F0.wireOp",EDGE,"E1.left");var subQ10=sQuery(id+"F0.wireOp",EDGE,"E23.filletArc");var subQ11=sQuery(id+"F0.wireOp",EDGE,"E24.filletArc");Q0=makeQuery(id+"F2.boolean.opBoolean","SPLIT",FACE,{"disambiguationData":[TD([makeQuery(id+"F1.opExtrude","SWEPT_FACE",FACE,{"disambiguationData":[OSD([subQ6])]})])],"derivedFrom":makeQuery(id+"F1.opExtrude","CAP_FACE",FACE,{"disambiguationData":[OSD([subQ6,subQ8,subQ9,subQ7,subQ4,subQ3,subQ2,subQ1,subQ0,subQ5,subQ10,subQ11])],"isStart":true})});}
            var sketch = newSketch(context, id + "F16", { "sketchPlane" : qUnion([Q0])});
            skSolve(sketch);
        }
        {
            var Q0;
            Q0=makeQuery(id+"F16.imprint","IMPRINT",FACE,{"disambiguationData":[TD([[makeQuery(id+"F16.imprint","IMPRINT",EDGE,{"derivedFrom":makeQuery(id+"F1.opExtrude","CAP_EDGE",EDGE,{"disambiguationData":[OSD([sQuery(id+"F0.wireOp",EDGE,"E1.bottom")])],"isStart":true})}),1.0]])]});
            var sketch = newSketch(context, id + "F17", { "sketchPlane" : qUnion([Q0])});
            skLineSegment(sketch, "E79.0.0", {"start": v(70, 90) * mm, "end": v(-70, 90) * mm});
            skArc(sketch, "E79.0.1", {"start": v(-70, 90) * mm, "mid": v(-77.07, 87.07) * mm, "end": v(-80, 80) * mm});
            skLineSegment(sketch, "E79.0.2", {"start": v(-80, 80) * mm, "end": v(-80, -80) * mm});
            skArc(sketch, "E79.0.3", {"start": v(-80, -80) * mm, "mid": v(-77.07, -87.07) * mm, "end": v(-70, -90) * mm});
            skLineSegment(sketch, "E79.0.4", {"start": v(-70, -90) * mm, "end": v(70, -90) * mm});
            skArc(sketch, "E79.0.5", {"start": v(70, -90) * mm, "mid": v(77.07, -87.07) * mm, "end": v(80, -80) * mm});
            skLineSegment(sketch, "E79.0.6", {"start": v(80, -80) * mm, "end": v(80, 80) * mm});
            skArc(sketch, "E79.0.7", {"start": v(80, 80) * mm, "mid": v(77.07, 87.07) * mm, "end": v(70, 90) * mm});
            skLineSegment(sketch, "E80", {"start": v(0, 90) * mm, "end": v(0, 120) * mm, "construction": true});
            skPoint(sketch, "E80.endSnap0", {"position": v(0, 90) * mm});
            skCircle(sketch, "E81", {"center": v(0, 120) * mm, "radius": 6 * mm});
            skArc(sketch, "E82", {"start": v(15, 120) * mm, "mid": v(0, 135) * mm, "end": v(-15, 120) * mm});
            skLineSegment(sketch, "E83", {"start": v(-15, 120) * mm, "end": v(-15, 108) * mm});
            skLineSegment(sketch, "E84", {"start": v(15, 108) * mm, "end": v(15, 104.27) * mm});
            skLineSegment(sketch, "E85", {"start": v(15, 108) * mm, "end": v(33, 90) * mm});
            skLineSegment(sketch, "E86", {"start": v(-15, 108) * mm, "end": v(-33, 90) * mm});
            skLineSegment(sketch, "E87.MirrorCS", {"start": v(15, 120) * mm, "end": v(15, 108) * mm});
            skArc(sketch, "E88.MirrorCS", {"start": v(-15, 120) * mm, "mid": v(0, 135) * mm, "end": v(15, 120) * mm});
            skLineSegment(sketch, "E89.MirrorCS", {"start": v(-15, 108) * mm, "end": v(-15, 104.27) * mm});
            skLineSegment(sketch, "E90", {"start": v(-80, 0) * mm, "end": v(80, 0) * mm, "construction": true});
            skArc(sketch, "E91.MirrorCS", {"start": v(-15, -120) * mm, "mid": v(0, -135) * mm, "end": v(15, -120) * mm});
            skLineSegment(sketch, "E92.MirrorCS", {"start": v(15, -120) * mm, "end": v(15, -108) * mm});
            skLineSegment(sketch, "E93.MirrorCS", {"start": v(-15, -120) * mm, "end": v(-15, -108) * mm});
            skLineSegment(sketch, "E94.MirrorCS", {"start": v(-15, -108) * mm, "end": v(-33, -90) * mm});
            skLineSegment(sketch, "E95.MirrorCS", {"start": v(15, -108) * mm, "end": v(33, -90) * mm});
            skLineSegment(sketch, "E96.MirrorCS", {"start": v(0, -90) * mm, "end": v(0, -120) * mm, "construction": true});
            skCircle(sketch, "E97.MirrorC", {"center": v(0, -120) * mm, "radius": 6 * mm});
            skSolve(sketch);
        }
        {
            var Q0;
            {var subQ1=sQuery(id+"F17.wireOp",EDGE,"E86");Q0=makeQuery(id+"F17.imprint","IMPRINT",FACE,{"disambiguationData":[TD([[makeQuery(id+"F17.imprint","IMPRINT",EDGE,{"derivedFrom":subQ1}),1.0]])]});}
            var Q1;
            Q1=makeQuery(id+"F16.imprint","IMPRINT",FACE,{"disambiguationData":[TD([[makeQuery(id+"F16.imprint","IMPRINT",EDGE,{"derivedFrom":makeQuery(id+"F1.opExtrude","CAP_EDGE",EDGE,{"disambiguationData":[OSD([sQuery(id+"F0.wireOp",EDGE,"E1.bottom")])],"isStart":true})}),1.0]])]});
            var Q2;
            Q2=makeQuery(id+"F17.imprint","IMPRINT",FACE,{"disambiguationData":[TD([[makeQuery(id+"F17.imprint","IMPRINT",EDGE,{"derivedFrom":sQuery(id+"F17.wireOp",EDGE,"E91.MirrorCS")}),1.0]])]});
            var Q3;
            Q3=makeQuery(id+"F2.opExtrude","CAP_FACE",FACE,{"disambiguationData":[OSD([sQuery(id+"F0.wireOp",EDGE,"E12"),sQuery(id+"F0.wireOp",EDGE,"E13"),sQuery(id+"F0.wireOp",EDGE,"E14"),sQuery(id+"F0.wireOp",EDGE,"E15"),sQuery(id+"F0.wireOp",EDGE,"E17.filletArc"),sQuery(id+"F0.wireOp",EDGE,"E18.filletArc"),sQuery(id+"F0.wireOp",EDGE,"E19.filletArc"),sQuery(id+"F0.wireOp",EDGE,"E20.filletArc"),sQuery(id+"F0.wireOp",EDGE,"E25.0"),sQuery(id+"F0.wireOp",EDGE,"E25.1"),sQuery(id+"F0.wireOp",EDGE,"E25.2"),sQuery(id+"F0.wireOp",EDGE,"E25.3"),sQuery(id+"F0.wireOp",EDGE,"E25.4"),sQuery(id+"F0.wireOp",EDGE,"E25.5"),sQuery(id+"F0.wireOp",EDGE,"E25.6"),sQuery(id+"F0.wireOp",EDGE,"E25.7")])],"isStart":false});
            extrude(context, id + "F18", {"entities" : qUnion([Q0, Q1, Q2]), "endBound" : BoundingType.UP_TO_SURFACE, "endBoundEntityFace" : qUnion([Q3]), "depth" : 25 * mm});
        }
    });
